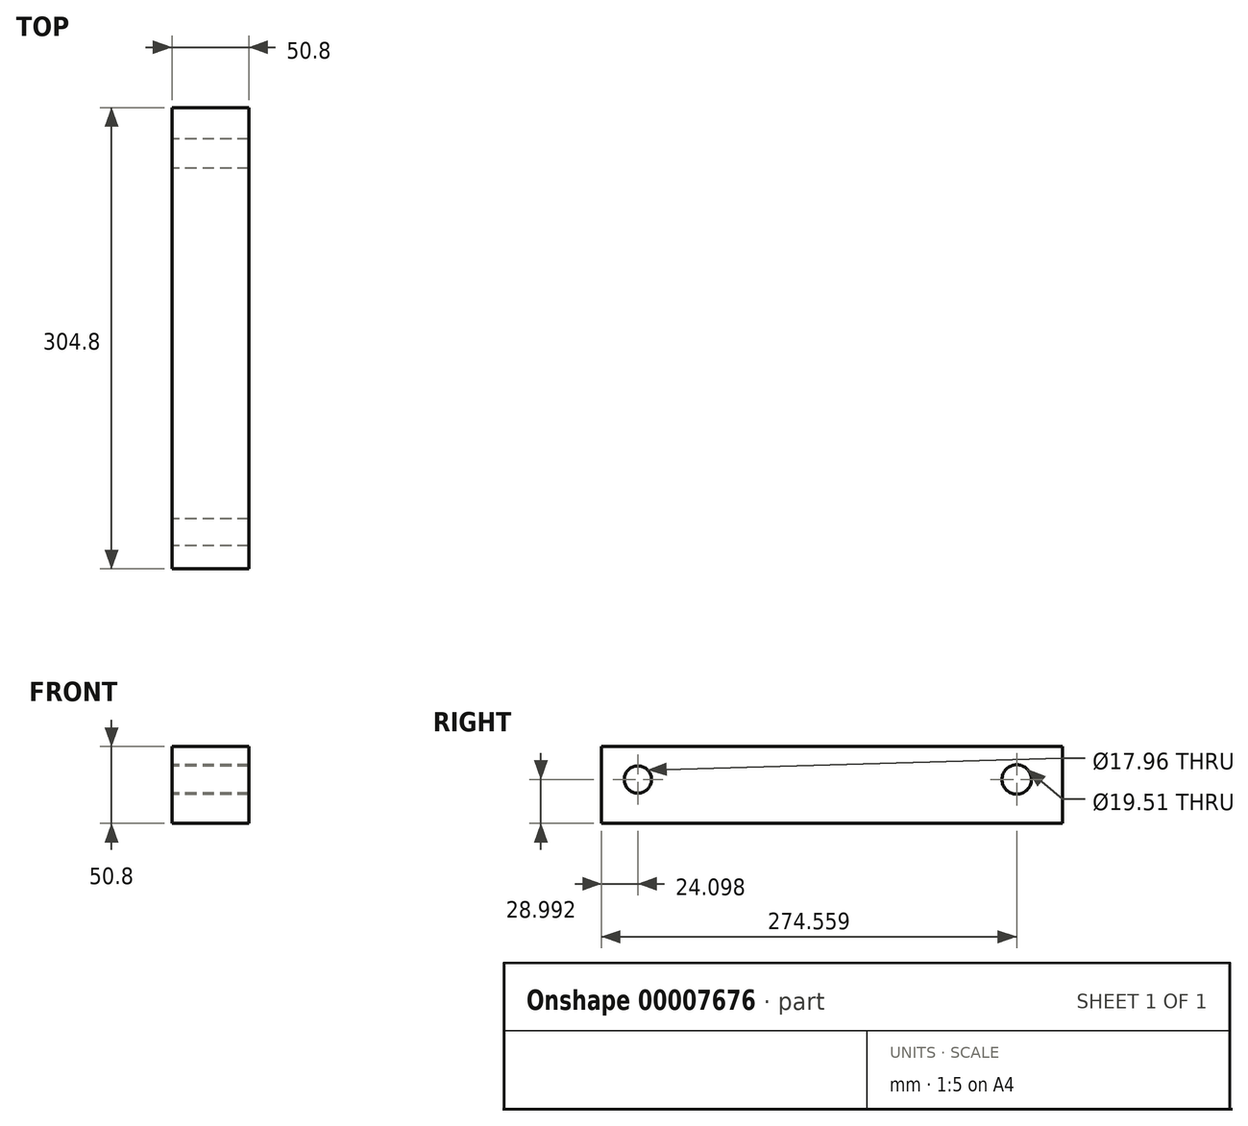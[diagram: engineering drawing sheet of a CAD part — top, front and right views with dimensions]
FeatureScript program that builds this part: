
annotation { "Feature Type Name" : "Feature", "Feature Type Description" : "" }
export const myFeature = defineFeature(function(context is Context, id is Id, definition is map)
    precondition{}
    {
        {
            var Q0;
            Q0=qCreatedBy(makeId("Front.planeOp"),FACE);
            var sketch = newSketch(context, id + "F0", { "sketchPlane" : qUnion([Q0])});
            skLineSegment(sketch, "E0.bottom", {"start": v(0, 0) * mm, "end": v(50.8, 0) * mm});
            skLineSegment(sketch, "E0.top", {"start": v(0, 50.8) * mm, "end": v(50.8, 50.8) * mm});
            skLineSegment(sketch, "E0.left", {"start": v(0, 0) * mm, "end": v(0, 50.8) * mm});
            skLineSegment(sketch, "E0.right", {"start": v(50.8, 0) * mm, "end": v(50.8, 50.8) * mm});
            skSolve(sketch);
        }
        {
            var Q0;
            Q0 = qSketchRegion(id + "F0", true);
            extrude(context, id + "F1", {"entities" : qUnion([Q0]), "depth" : 304.8 * mm});
        }
        {
            var Q0;
            Q0=qCreatedBy(makeId("Right.planeOp"),FACE);
            var sketch = newSketch(context, id + "F2", { "sketchPlane" : qUnion([Q0])});
            skCircle(sketch, "E1", {"center": v(-30.24, 29) * mm, "radius": 9.75 * mm});
            skCircle(sketch, "E2", {"center": v(-280.7, 29) * mm, "radius": 8.98 * mm});
            skSolve(sketch);
        }
        {
            var Q0;
            Q0 = qSketchRegion(id + "F2", true);
            extrude(context, id + "F3", {"entities" : qUnion([Q0]), "operationType" : NewBodyOperationType.REMOVE, "depth" : 57.94 * mm});
        }
    });
